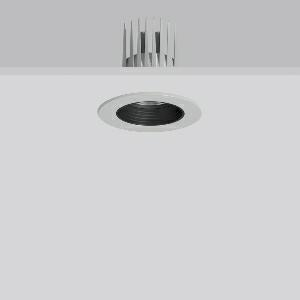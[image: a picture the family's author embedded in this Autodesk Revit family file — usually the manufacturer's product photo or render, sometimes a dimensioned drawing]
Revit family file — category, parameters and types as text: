
# Revit family: heledon_mini_e_901745_004_76_0de5
name_source: partatom
category: Lighting Fixtures
units: mm (PartAtom-declared; Revit-internal decimal feet)

## family parameters
Cut with Voids When Loaded = No
Host = Face
Light Source = No
Part Type = Normal
Room Calculation Point = No
Round Connector Dimension = Use Diameter
Shared = No

## types (1)
- HELEDON mini E (1 x LED Modul 930, 2000 lm, 3000)
    Apparent Load = 20 VA
    Approval mark = CE
    CIE Flux Codes = 98 100 100 100 100
    Color Rendering = 90
    Color Temperature = 3000
    Default Elevation = 1800 mm
    Description = Series: HELEDON mini
Round recessed downlight. Housing: die-cast aluminium, powder-coated. Black plastic ring and recessed LED to prevent glare from the side. Optical assembly with lens made of plastic (polycarbonate) for the best homogeneous light distribution - can be changed without tools. Best colour rendering index Ra>90. Suitable for Recessed ceiling mounting. Installation without tools thanks to spring fastening system. Including separate LED converter with connecting cable 600 mm.High quality converter without flickering and stroboscopic effect. Through-wiring box (5 pole) available as accessory. The following accessories can be mounted without use of tools: interchangeable lenses, decorative glasses, honeycomb louvre, clear and frosted diffusers, white interchangeable plastic ring. 
Colour: silver
Diameter: 124 mm
Height: 3 mm
Cut-out diameter: 114 mm
Recess height: 170 mm
Luminaire: recess height: 120 mm
Lamp: LED
Socket: without socket
Colour temperature: 3000K
Colour rendering index (CRI): 92
System power: 20 W
Rated luminous flux: 2000 lm
Luminous efficiency: 100 lm/W
Control gear: Converter, dimmable, DALI
Protection class: II
Type of protection: IP 20
    Height = 0 mm  [stored 0 ft]
    Lamp = 1 x LED Modul 930
    Lamp Light Flux = 2000 lm
    Lamp count = 1
    Length = 124 mm  [stored 0.406824 ft]
    Lifetime = 50000 h
    Luminous efficacy = 100 lm/W
    Manufacturer = RZB
    ModVariant = No
    Model = 901745.004.76
    Mounting Place = Ceiling
    Mounting Type = Recessed
    Number of Poles = 1
    OnlyDefault = Yes
    Power Factor = 1
    Product Name = HELEDON mini E
    Product group = Recessed downlights
    ProductGroupID = 402
    Protection Class = Protection class II
    Protection Degree = IP 20
    RLX_Detail_Level = 1
    RLX_Emergency_Light_Flux = 0 lm
    RLX_Emergency_Type = 0
    RLX_Emergency_Type_DB = No
    RlxData = <blob elided: 124165 chars, md5=cd711983>
    Socket = socket
    Standby Power = 0 W
    System Light Flux = 2000 lm
    System Power = 20 W
    Type Comments = Product without accessories
    Type Image = 901656.004.jpg
    URL = http://relux.com
    VarID = ---
    Voltage = 230 V
    Voltage Range = 220-240 V
    Weight = 0.00 kg
    Width = 0 mm  [stored 0 ft]

note: [stored X ft] marks values corroborated as IEEE doubles in the binary element streams (Revit-internal decimal feet)

## geometry (parser evidence)
native form markers: Blend x4, Sweep x11
no freeform markers — native parametric forms only
